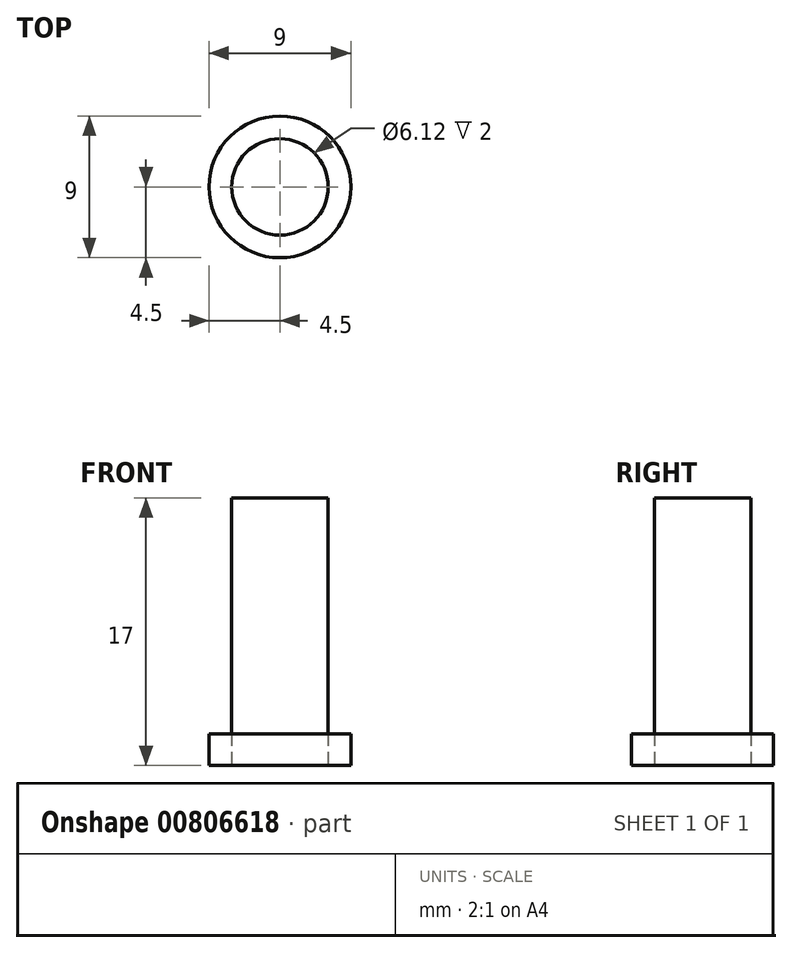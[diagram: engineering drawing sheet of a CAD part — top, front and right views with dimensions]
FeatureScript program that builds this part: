
annotation { "Feature Type Name" : "Feature", "Feature Type Description" : "" }
export const myFeature = defineFeature(function(context is Context, id is Id, definition is map)
    precondition{}
    {
        {
            var Q0;
            Q0=qCreatedBy(makeId("Top.planeOp"),FACE);
            var sketch = newSketch(context, id + "F0", { "sketchPlane" : qUnion([Q0])});
            skCircle(sketch, "E0", {"center": v(0, 0) * mm, "radius": 3.06 * mm});
            skCircle(sketch, "E1", {"center": v(0, 0) * mm, "radius": 4.5 * mm});
            skSolve(sketch);
        }
        {
            var Q0;
            Q0=makeQuery(id+"F0.imprint","IMPRINT",FACE,{"disambiguationData":[TD([[makeQuery(id+"F0.imprint","IMPRINT",EDGE,{"derivedFrom":sQuery(id+"F0.wireOp",EDGE,"E0")}),1.0]])]});
            var Q1;
            Q1=sQuery(id+"F0.wireOp",EDGE,"E0");
            extrude(context, id + "F1", {"entities" : qUnion([Q0]), "surfaceEntities" : qUnion([Q1]), "depth" : 17 * mm, "offsetDistance" : 25 * mm});
        }
        {
            var Q0;
            Q0 = qSketchRegion(id + "F0", true);
            extrude(context, id + "F2", {"entities" : qUnion([Q0]), "depth" : 2 * mm, "offsetDistance" : 25 * mm});
        }
    });
